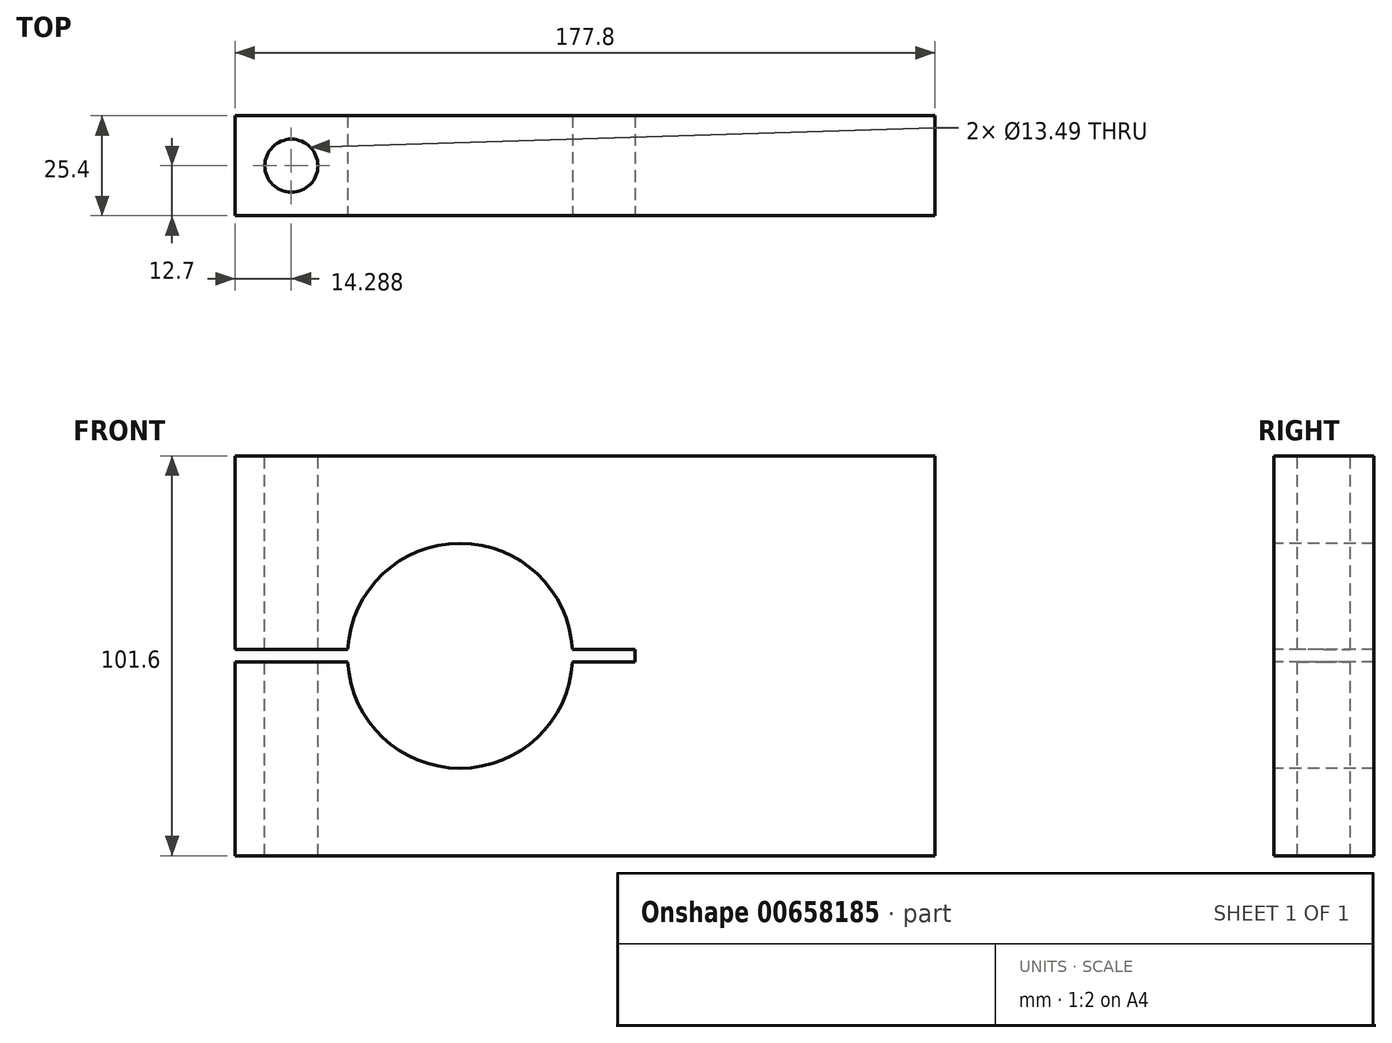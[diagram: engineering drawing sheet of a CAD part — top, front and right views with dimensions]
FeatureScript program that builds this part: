
annotation { "Feature Type Name" : "Feature", "Feature Type Description" : "" }
export const myFeature = defineFeature(function(context is Context, id is Id, definition is map)
    precondition{}
    {
        {
            var Q0;
            Q0=qCreatedBy(makeId("Front.planeOp"),FACE);
            var sketch = newSketch(context, id + "F0", { "sketchPlane" : qUnion([Q0])});
            skLineSegment(sketch, "E0.bottom", {"start": v(-88.9, -50.8) * mm, "end": v(88.9, -50.8) * mm});
            skLineSegment(sketch, "E0.top", {"start": v(-88.9, 50.8) * mm, "end": v(88.9, 50.8) * mm});
            skLineSegment(sketch, "E0.left", {"start": v(-88.9, -50.8) * mm, "end": v(-88.9, 50.8) * mm});
            skLineSegment(sketch, "E0.right", {"start": v(88.9, -50.8) * mm, "end": v(88.9, 50.8) * mm});
            skPoint(sketch, "E0.middle", {"position": v(0, 0) * mm});
            skCircle(sketch, "E1", {"center": v(-31.75, 0) * mm, "radius": 28.58 * mm});
            skPoint(sketch, "E1.centerSnap0", {"position": v(-88.9, 0) * mm});
            skLineSegment(sketch, "E2", {"start": v(-88.9, 1.59) * mm, "end": v(12.7, 1.59) * mm});
            skLineSegment(sketch, "E3", {"start": v(12.7, 1.59) * mm, "end": v(12.7, 0) * mm});
            skLineSegment(sketch, "E4.MirrorCS", {"start": v(-88.9, -1.59) * mm, "end": v(12.7, -1.59) * mm});
            skLineSegment(sketch, "E5.MirrorCS", {"start": v(12.7, -1.59) * mm, "end": v(12.7, 0) * mm});
            skSolve(sketch);
        }
        {
            var Q0;
            {var subQ9=sQuery(id+"F0.wireOp",EDGE,"E0.bottom");Q0=makeQuery(id+"F0.imprint","IMPRINT",FACE,{"disambiguationData":[TD([[makeQuery(id+"F0.imprint","IMPRINT",EDGE,{"derivedFrom":subQ9}),1.0]])]});}
            extrude(context, id + "F1", {"entities" : qUnion([Q0]), "oppositeDirection" : true, "depth" : 25.4 * mm, "offsetDistance" : 25.4 * mm});
        }
        {
            var Q0;
            Q0=makeQuery(id+"F1.opExtrude","SWEPT_FACE",FACE,{"disambiguationData":[OSD([sQuery(id+"F0.wireOp",EDGE,"E0.top")])]});
            var sketch = newSketch(context, id + "F2", { "sketchPlane" : qUnion([Q0])});
            skPoint(sketch, "E6", {"position": v(-74.61, 12.7) * mm});
            skPoint(sketch, "E6.positionSnap0", {"position": v(-88.9, 12.7) * mm});
            skSolve(sketch);
        }
        {
            var Q0;
            Q0=sQuery(id+"F2.wireOp",VERTEX,"E6");
            var Q1;
            Q1=makeQuery(id+"F1.opExtrude","SWEPT_BODY",BODY,{"disambiguationData":[OSD([sQuery(id+"F0.wireOp",EDGE,"E0.bottom"),sQuery(id+"F0.wireOp",EDGE,"E0.top"),sQuery(id+"F0.wireOp",EDGE,"E0.left"),sQuery(id+"F0.wireOp",EDGE,"E0.right"),sQuery(id+"F0.wireOp",EDGE,"E1"),sQuery(id+"F0.wireOp",EDGE,"E2"),sQuery(id+"F0.wireOp",EDGE,"E3"),sQuery(id+"F0.wireOp",EDGE,"E4.MirrorCS"),sQuery(id+"F0.wireOp",EDGE,"E5.MirrorCS")])]});
            hole(context, id + "F3", {"style" : HoleStyle.SIMPLE, "endStyle" : HoleEndStyle.THROUGH, "standardTappedOrClearance" : lookupTablePath({ "standard" : "ANSI", "fit" : "Normal (ASME)", "size" : "1/2", "type" : "Clearance" }), "standardBlindInLast" : lookupTablePath({ "fit" : "Free", "standard" : "ANSI", "size" : "1/2", "type" : "Clearance" }), "holeDiameter" : 13.5 * mm, "majorDiameter" : 6.35 * mm, "isTappedThrough" : true, "tappedDepth" : 12.7 * mm, "tapClearance" : 3, "locations" : qUnion([Q0]), "scope" : qUnion([Q1])});
        }
    });
